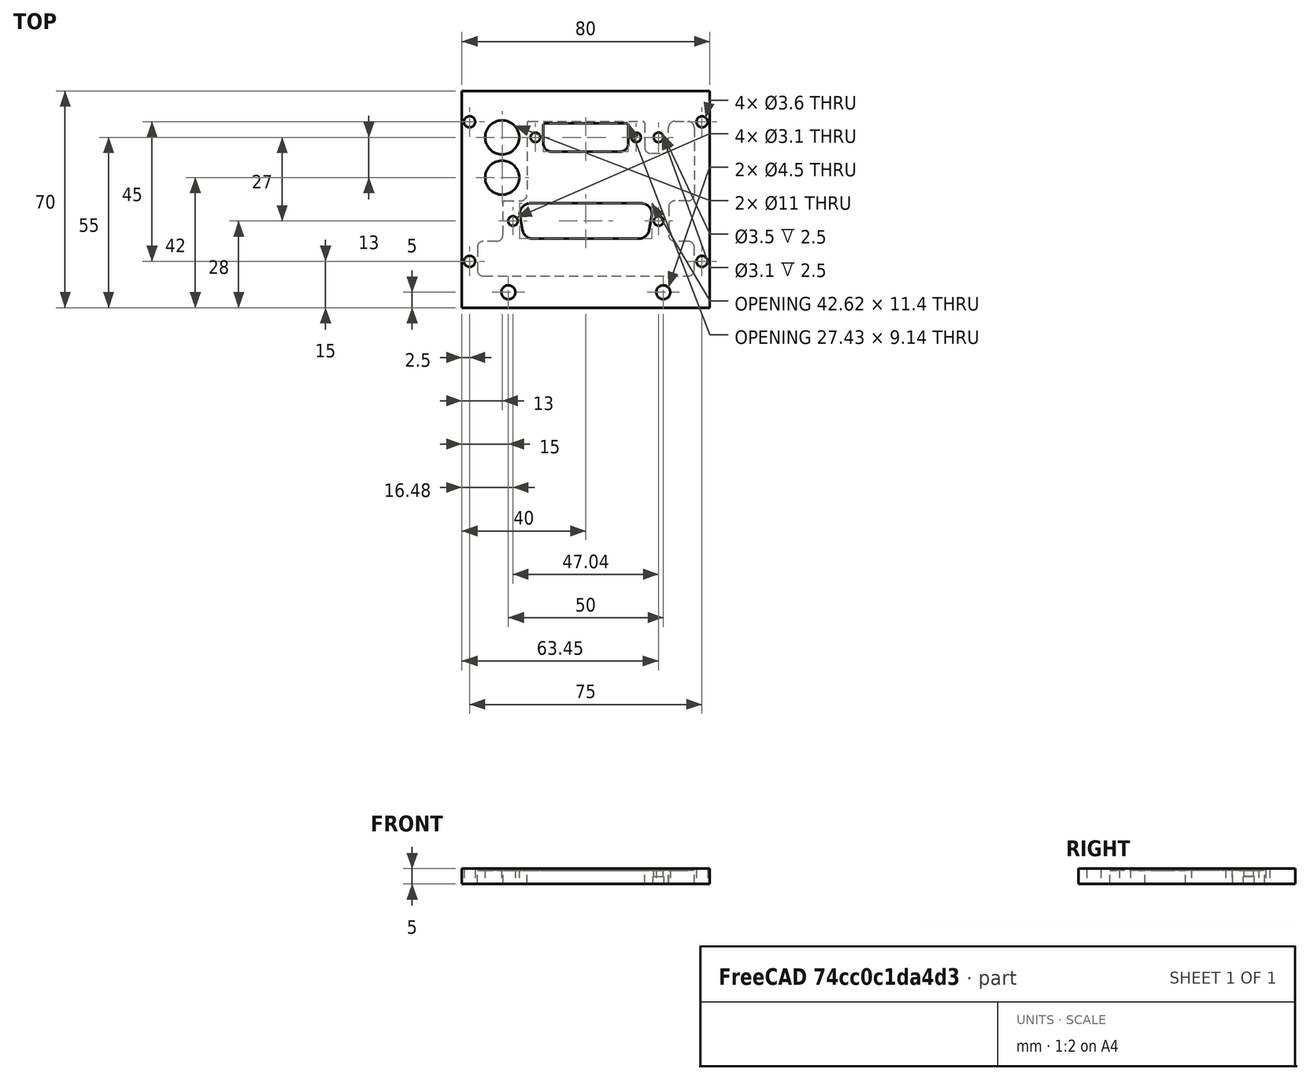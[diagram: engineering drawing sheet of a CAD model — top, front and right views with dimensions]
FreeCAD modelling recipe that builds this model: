
FCSTD DOCUMENT  (FreeCAD 1.0R39319 (Git))
Label: back_panel
License: CERN Open Hardware Licence weakly-reciprocal
LicenseURL: https://cern-ohl.web.cern.ch/
objects: TechDraw::DrawViewDimension×45, Sketcher::SketchObject×8, PartDesign::Hole×5, TechDraw::DrawProjGroupItem×5, TechDraw::DrawSVGTemplate×3, TechDraw::DrawPage×3, PartDesign::Pocket×2, TechDraw::DrawProjGroup×2, PartDesign::Pad×1, PartDesign::Body×1, TechDraw::DrawViewImage×1, TechDraw::DrawViewAnnotation×1, TechDraw::DrawViewSymbol×1
note: 118 computed .brp shape members not serialized (recipe doc carries the construction recipe); baked Part::Feature solids carry a one-line shape summary decoded from their .brp

FEATURE [Sketcher::SketchObject] Sketch
  ArcFitTolerance = 1e-06
  AttachmentSupport = -> [XY_Plane]
  FullyConstrained = true
  MakeInternals = false
  MapMode = 5
  sketch-geometry (5):
    g0: LineSegment StartX=-40 StartY=-35 StartZ=0 EndX=40 EndY=-35 EndZ=0
    g1: LineSegment StartX=40 StartY=-35 StartZ=0 EndX=40 EndY=35 EndZ=0
    g2: LineSegment StartX=40 StartY=35 StartZ=0 EndX=-40 EndY=35 EndZ=0
    g3: LineSegment StartX=-40 StartY=35 StartZ=0 EndX=-40 EndY=-35 EndZ=0
    g4: GeomPoint [constr] X=0 Y=0 Z=0
  constraints (12):
    c: Coincident(g0,g1)
    c: Coincident(g1,g2)
    c: Coincident(g2,g3)
    c: Coincident(g3,g0)
    c: Horizontal(g0)
    c: Horizontal(g2)
    c: Vertical(g1)
    c: Vertical(g3)
    c: Symmetric(g2,g0,g4)
    c: Distance(g1,g3) = 80
    c: Distance(g0,g2) = 70
    c: Coincident(g4,g-1)
FEATURE [PartDesign::Pad] Pad
  Direction = (0,0,1)
  Length = 5
  Length2 = 10
  Profile = -> Sketch
  ReferenceAxis = -> Sketch [N_Axis]
  Suppressed = false
  Type = 0
FEATURE [Sketcher::SketchObject] Sketch001
  ArcFitTolerance = 1e-06
  AttachmentSupport = -> [Pad]
  FullyConstrained = true
  MakeInternals = false
  MapMode = 5
  Placement = pos=(0,0,5) rot=(0,0,1;0rad)
  sketch-geometry (4):
    g0: Circle CenterX=-37.5 CenterY=25 CenterZ=0 NormalX=0 NormalY=0 NormalZ=1 AngleXU=0 Radius=1.7
    g1: Circle CenterX=37.5 CenterY=25 CenterZ=0 NormalX=0 NormalY=0 NormalZ=1 AngleXU=0 Radius=1.7
    g2: Circle CenterX=-37.5 CenterY=-20 CenterZ=0 NormalX=0 NormalY=0 NormalZ=1 AngleXU=0 Radius=1.7
    g3: Circle CenterX=37.5 CenterY=-20 CenterZ=0 NormalX=0 NormalY=0 NormalZ=1 AngleXU=0 Radius=1.7
  constraints (10):
    c: DistanceX(g0,g-1) = 37.5
    c: DistanceY(g-1,g0) = 25
    c: Diameter(g0) = 3.4
    c: Symmetric(g0,g1,g-2)
    c: Equal(g1,g0)
    c: Symmetric(g2,g3,g-2)
    c: Equal(g2,g3)
    c: Equal(g3,g0)
    c: Vertical(g0,g2)
    c: DistanceY(g2,g-1) = 20
FEATURE [PartDesign::Hole] Hole
  BaseFeature = -> Pad
  CustomThreadClearance = 0
  Depth = 214.966
  DepthType = 1
  Diameter = 3.6
  DrillForDepth = false
  DrillPoint = 1
  DrillPointAngle = 118
  HoleCutCountersinkAngle = 90
  HoleCutCustomValues = false
  HoleCutDepth = 0
  HoleCutDiameter = 6.1
  HoleCutType = 0
  ModelThread = false
  Profile = -> Sketch001
  Suppressed = false
  Tapered = false
  TaperedAngle = 90
  ThreadClass = 0
  ThreadDepth = 214.966
  ThreadDepthType = 0
  ThreadDirection = 0
  ThreadFit = 2
  ThreadSize = 9
  ThreadType = 1
  Threaded = false
  UseCustomThreadClearance = false
FEATURE [Sketcher::SketchObject] Sketch005
  ArcFitTolerance = 1e-06
  AttachmentSupport = -> [Hole]
  FullyConstrained = true
  MakeInternals = false
  MapMode = 5
  Placement = pos=(0,0,5) rot=(0,0,1;0rad)
  sketch-geometry (2):
    g0: Circle CenterX=-25 CenterY=-30 CenterZ=0 NormalX=0 NormalY=0 NormalZ=1 AngleXU=0 Radius=2.25
    g1: Circle CenterX=25 CenterY=-30 CenterZ=0 NormalX=0 NormalY=0 NormalZ=1 AngleXU=0 Radius=2.25
  constraints (5):
    c: Symmetric(g1,g0,g-2)
    c: Equal(g0,g1)
    c: DistanceX(g0,g1) = 50
    c: DistanceY(g1,g-1) = 30
    c: Diameter(g0) = 4.5
FEATURE [PartDesign::Hole] Hole003
  BaseFeature = -> Hole
  CustomThreadClearance = 0
  Depth = 214.966
  DepthType = 1
  Diameter = 4.5
  DrillForDepth = false
  DrillPoint = 1
  DrillPointAngle = 118
  HoleCutCountersinkAngle = 90
  HoleCutCustomValues = false
  HoleCutDepth = 0
  HoleCutDiameter = 6.1
  HoleCutType = 0
  ModelThread = false
  Profile = -> Sketch005
  Suppressed = false
  Tapered = false
  TaperedAngle = 90
  ThreadClass = 0
  ThreadDepth = 214.966
  ThreadDepthType = 0
  ThreadDirection = 0
  ThreadFit = 0
  ThreadSize = 0
  ThreadType = 0
  Threaded = false
  UseCustomThreadClearance = false
FEATURE [Sketcher::SketchObject] Sketch003
  ArcFitTolerance = 1e-06
  AttachmentSupport = -> [Hole003]
  FullyConstrained = true
  MakeInternals = false
  MapMode = 5
  Placement = pos=(0,0,5) rot=(0,0,1;0rad)
  sketch-geometry (4):
    g0: Circle CenterX=-16.255 CenterY=20 CenterZ=0 NormalX=0 NormalY=0 NormalZ=1 AngleXU=0 Radius=1.525
    g1: Circle CenterX=16.255 CenterY=20 CenterZ=0 NormalX=0 NormalY=0 NormalZ=1 AngleXU=0 Radius=1.525
    g2: Circle CenterX=-23.52 CenterY=-7 CenterZ=0 NormalX=0 NormalY=0 NormalZ=1 AngleXU=0 Radius=1.525
    g3: Circle CenterX=23.52 CenterY=-7 CenterZ=0 NormalX=0 NormalY=0 NormalZ=1 AngleXU=0 Radius=1.525
  constraints (10):
    c: Diameter(g0) = 3.05
    c: Equal(g1,g0)
    c: DistanceX(g0,g1) = 32.51
    c: DistanceY(g-1,g1) = 20
    c: Equal(g0,g2)
    c: Equal(g2,g3)
    c: DistanceX(g2,g3) = 47.04
    c: DistanceY(g3,g-1) = 7
    c: Symmetric(g0,g1,g-2)
    c: Symmetric(g2,g3,g-2)
FEATURE [PartDesign::Hole] Hole001
  BaseFeature = -> Hole003
  CustomThreadClearance = 0
  Depth = 214.966
  DepthType = 1
  Diameter = 3.1
  DrillForDepth = false
  DrillPoint = 1
  DrillPointAngle = 118
  HoleCutCountersinkAngle = 90
  HoleCutCustomValues = false
  HoleCutDepth = 0
  HoleCutDiameter = 6.1
  HoleCutType = 0
  ModelThread = false
  Profile = -> Sketch003
  Suppressed = false
  Tapered = false
  TaperedAngle = 90
  ThreadClass = 0
  ThreadDepth = 214.966
  ThreadDepthType = 0
  ThreadDirection = 0
  ThreadFit = 0
  ThreadSize = 0
  ThreadType = 0
  Threaded = false
  UseCustomThreadClearance = false
FEATURE [Sketcher::SketchObject] Sketch002
  ArcFitTolerance = 1e-06
  AttachmentSupport = -> [Hole001]
  ExternalGeometry = -> [Hole001]
  FullyConstrained = true
  MakeInternals = false
  MapMode = 5
  Placement = pos=(0,0,5) rot=(0,0,1;0rad)
  sketch-geometry (2):
    g0: Circle CenterX=-27 CenterY=7 CenterZ=0 NormalX=0 NormalY=0 NormalZ=1 AngleXU=0 Radius=5.5
    g1: Circle CenterX=-27 CenterY=20 CenterZ=0 NormalX=0 NormalY=0 NormalZ=1 AngleXU=0 Radius=5.5
  constraints (6):
    c: Equal(g1,g0)
    c: Vertical(g1,g0)
    c: DistanceY(g0,g1) = 13
    c: Diameter(g1) = 11
    c: DistanceX(g0,g-1) = 27
    c: Horizontal(g-3,g1)
FEATURE [PartDesign::Hole] Hole002
  BaseFeature = -> Hole001
  CustomThreadClearance = 0
  Depth = 25
  DepthType = 0
  Diameter = 11
  DrillForDepth = false
  DrillPoint = 1
  DrillPointAngle = 118
  HoleCutCountersinkAngle = 90
  HoleCutCustomValues = false
  HoleCutDepth = 0
  HoleCutDiameter = 6.1
  HoleCutType = 0
  ModelThread = false
  Profile = -> Sketch002
  Suppressed = false
  Tapered = false
  TaperedAngle = 90
  ThreadClass = 0
  ThreadDepth = 25
  ThreadDepthType = 0
  ThreadDirection = 0
  ThreadFit = 0
  ThreadSize = 0
  ThreadType = 0
  Threaded = false
  UseCustomThreadClearance = false
FEATURE [Sketcher::SketchObject] Sketch004
  ArcFitTolerance = 1e-06
  AttachmentSupport = -> [Hole002]
  ExternalGeometry = -> [Hole002]
  FullyConstrained = true
  MakeInternals = false
  MapMode = 5
  Placement = pos=(0,0,5) rot=(0,0,1;0rad)
  sketch-geometry (23):
    g0: LineSegment StartX=-13.715 StartY=23.94 StartZ=0 EndX=-13.715 EndY=17.97 EndZ=0
    g1: LineSegment StartX=-11.175 StartY=15.43 StartZ=0 EndX=11.175 EndY=15.43 EndZ=0
    g2: LineSegment StartX=13.715 StartY=17.97 StartZ=0 EndX=13.715 EndY=23.94 EndZ=0
    g3: LineSegment StartX=13.085 StartY=24.57 StartZ=0 EndX=-13.085 EndY=24.57 EndZ=0
    g4: ArcOfCircle CenterX=-13.085 CenterY=23.94 CenterZ=0 NormalX=0 NormalY=0 NormalZ=1 AngleXU=0 Radius=0.63 StartAngle=1.5708 EndAngle=3.14159
    g5: ArcOfCircle CenterX=-11.175 CenterY=17.97 CenterZ=0 NormalX=0 NormalY=0 NormalZ=1 AngleXU=0 Radius=2.54 StartAngle=3.14159 EndAngle=4.71239
    g6: ArcOfCircle CenterX=11.175 CenterY=17.97 CenterZ=0 NormalX=0 NormalY=0 NormalZ=1 AngleXU=0 Radius=2.54 StartAngle=4.71239 EndAngle=6.28319
    g7: ArcOfCircle CenterX=13.085 CenterY=23.94 CenterZ=0 NormalX=0 NormalY=0 NormalZ=1 AngleXU=0 Radius=0.63 StartAngle=2.2e-15 EndAngle=1.5708
    g8: GeomPoint [constr] X=-13.715 Y=24.57 Z=0
    g9: GeomPoint [constr] X=13.715 Y=15.43 Z=0
    g10: LineSegment StartX=-21.26 StartY=-5.23172 StartZ=0 EndX=-20.4313 EndY=-9.93172 EndZ=0
    g11: LineSegment StartX=-17.1322 StartY=-12.7 StartZ=0 EndX=17.1322 EndY=-12.7 EndZ=0
    g12: LineSegment StartX=20.4313 StartY=-9.93172 StartZ=0 EndX=21.26 EndY=-5.23172 EndZ=0
    g13: LineSegment StartX=17.9609 StartY=-1.3 StartZ=0 EndX=-17.9609 EndY=-1.3 EndZ=0
    g14: ArcOfCircle CenterX=-17.9609 CenterY=-4.65 CenterZ=0 NormalX=0 NormalY=0 NormalZ=1 AngleXU=0 Radius=3.35 StartAngle=1.5708 EndAngle=3.31613
    g15: ArcOfCircle CenterX=-17.1322 CenterY=-9.35 CenterZ=0 NormalX=0 NormalY=0 NormalZ=1 AngleXU=0 Radius=3.35 StartAngle=3.31613 EndAngle=4.71239
    g16: ArcOfCircle CenterX=17.1322 CenterY=-9.35 CenterZ=0 NormalX=0 NormalY=0 NormalZ=1 AngleXU=0 Radius=3.35 StartAngle=4.71239 EndAngle=6.10865
    g17: ArcOfCircle CenterX=17.9609 CenterY=-4.65 CenterZ=0 NormalX=0 NormalY=0 NormalZ=1 AngleXU=0 Radius=3.35 StartAngle=6.10865 EndAngle=7.85398
    g18: GeomPoint [constr] X=19.9431 Y=-12.7 Z=0
    g19: LineSegment [constr] StartX=16.255 StartY=20 StartZ=0 EndX=-16.255 EndY=20 EndZ=0
    g20: LineSegment [constr] StartX=-23.52 StartY=-7 StartZ=0 EndX=23.52 EndY=-7 EndZ=0
    g21: LineSegment [constr] StartX=-9e-16 StartY=-1.3 StartZ=0 EndX=-9e-16 EndY=-12.7 EndZ=0
    g22: GeomPoint [constr] X=13.715 Y=24.57 Z=0
  constraints (51):
    c: Tangent(g0,g4) = -1.5708
    c: Tangent(g0,g5) = -1.5708
    c: Tangent(g1,g5) = -1.5708
    c: Tangent(g1,g6) = -1.5708
    c: Tangent(g2,g6) = -1.5708
    c: Tangent(g2,g7) = -1.5708
    c: Tangent(g3,g7) = -1.5708
    c: Tangent(g3,g4) = -1.5708
    c: Vertical(g0)
    c: Horizontal(g1)
    c: Horizontal(g3)
    c: PointOnObject(g8,g0)
    c: PointOnObject(g8,g3)
    c: PointOnObject(g9,g1)
    c: PointOnObject(g9,g2)
    c: Radius(g5) = 2.54
    c: Radius(g4) = 0.63
    c: Distance(g1,g3) = 9.14
    c: Tangent(g10,g14) = -1.5708
    c: Tangent(g10,g15) = -1.5708
    c: Tangent(g11,g15) = -1.5708
    c: Tangent(g11,g16) = -1.5708
    c: Tangent(g12,g16) = -1.5708
    c: Tangent(g12,g17) = -1.5708
    c: Tangent(g13,g17) = -1.5708
    c: Tangent(g13,g14) = -1.5708
    c: Horizontal(g11)
    c: Horizontal(g13)
    c: Equal(g15,g16)
    c: PointOnObject(g18,g11)
    c: PointOnObject(g18,g12)
    c: Symmetric(g12,g10,g-2)
    c: Radius(g14) = 3.35
    c: Equal(g14,g17)
    c: DistanceY(g11,g13) = 11.4
    c: DistanceX(g10,g12) = 42.52
    c: Equal(g17,g15)
    c: Coincident(g19,g-4)
    c: Coincident(g19,g-3)
    c: Coincident(g20,g-5)
    c: Coincident(g20,g-6)
    c: Symmetric(g0,g2,g-2)
    c: Equal(g7,g4)
    c: PointOnObject(g21,g13)
    c: Symmetric(g21,g21,g20)
    c: Symmetric(g11,g11,g21)
    c: DistanceX(g0,g2) = 27.43
    c: PointOnObject(g22,g2)
    c: PointOnObject(g22,g3)
    c: Symmetric(g22,g9,g19)
    c: Angle(g12,g-2) = 0.174533
FEATURE [PartDesign::Pocket] Pocket
  BaseFeature = -> Hole002
  Direction = (0,0,-1)
  Length = 5
  Length2 = 5
  Profile = -> Sketch004
  ReferenceAxis = -> Sketch004 [N_Axis]
  Suppressed = false
  Type = 1
FEATURE [Sketcher::SketchObject] Sketch006
  ArcFitTolerance = 1e-06
  AttachmentSupport = -> [Pocket]
  ExternalGeometry = -> [Pocket]
  FullyConstrained = true
  MakeInternals = false
  MapMode = 5
  Placement = pos=(0,0,0) rot=(1,0,0;3.14159rad)
  sketch-geometry (1):
    g0: Circle CenterX=23.45 CenterY=-20 CenterZ=0 NormalX=0 NormalY=0 NormalZ=1 AngleXU=0 Radius=1.75
  constraints (3):
    c: Diameter(g0) = 3.5
    c: Horizontal(g0,g-3)
    c: DistanceX(g-1,g0) = 23.45
FEATURE [PartDesign::Hole] Hole004
  BaseFeature = -> Pocket
  CustomThreadClearance = 0
  Depth = 214.966
  DepthType = 1
  Diameter = 3.1
  DrillForDepth = false
  DrillPoint = 1
  DrillPointAngle = 118
  HoleCutCountersinkAngle = 90
  HoleCutCustomValues = false
  HoleCutDepth = 2.5
  HoleCutDiameter = 3.5
  HoleCutType = 1
  ModelThread = false
  Profile = -> Sketch006
  Suppressed = false
  Tapered = false
  TaperedAngle = 90
  ThreadClass = 0
  ThreadDepth = 214.966
  ThreadDepthType = 0
  ThreadDirection = 0
  ThreadFit = 0
  ThreadSize = 0
  ThreadType = 0
  Threaded = false
  UseCustomThreadClearance = false
FEATURE [Sketcher::SketchObject] Sketch007
  ArcFitTolerance = 1e-06
  AttachmentSupport = -> [Hole004]
  ExternalGeometry = -> [Hole004]
  FullyConstrained = true
  MakeInternals = false
  MapMode = 5
  Placement = pos=(0,0,0) rot=(1,0,0;3.14159rad)
  expr: Constraints[100] = 9.8 mm + 0.5 mm
  expr: Constraints[52] = 37.5 mm + 0.5 mm
  expr: Constraints[78] = 12.55 mm + 0.5 mm
  sketch-geometry (55):
    g0: LineSegment StartX=-18.4 StartY=-25.15 StartZ=0 EndX=18.4 EndY=-25.15 EndZ=0
    g1: LineSegment StartX=19 StartY=-24.55 StartZ=0 EndX=19 EndY=-16.85 EndZ=0
    g2: LineSegment StartX=26.75 StartY=2.475 StartZ=0 EndX=26.75 EndY=11.525 EndZ=0
    g3: LineSegment StartX=-26.75 StartY=11.525 StartZ=0 EndX=-26.75 EndY=1.075 EndZ=0
    g4: LineSegment StartX=-26.15 StartY=0.475 StartZ=0 EndX=-21 EndY=0.475 EndZ=0
    g5: LineSegment StartX=-19 StartY=-24.55 StartZ=0 EndX=-19 EndY=-1.525 EndZ=0
    g6: ArcOfCircle CenterX=21 CenterY=-16.85 CenterZ=0 NormalX=0 NormalY=0 NormalZ=1 AngleXU=0 Radius=2 StartAngle=1.5708 EndAngle=3.14159
    g7: GeomPoint [constr] X=19 Y=-14.85 Z=0
    g8: ArcOfCircle CenterX=18.4 CenterY=-24.55 CenterZ=0 NormalX=0 NormalY=0 NormalZ=1 AngleXU=0 Radius=0.6 StartAngle=4.71239 EndAngle=6.28319
    g9: GeomPoint [constr] X=19 Y=-25.15 Z=0
    g10: ArcOfCircle CenterX=-18.4 CenterY=-24.55 CenterZ=0 NormalX=0 NormalY=0 NormalZ=1 AngleXU=0 Radius=0.6 StartAngle=3.14159 EndAngle=4.71239
    g11: GeomPoint [constr] X=-19 Y=-25.15 Z=0
    g12: ArcOfCircle CenterX=-21 CenterY=-1.525 CenterZ=0 NormalX=0 NormalY=0 NormalZ=1 AngleXU=0 Radius=2 StartAngle=0 EndAngle=1.5708
    g13: GeomPoint [constr] X=-19 Y=0.475 Z=0
    g14: ArcOfCircle CenterX=-26.15 CenterY=1.075 CenterZ=0 NormalX=0 NormalY=0 NormalZ=1 AngleXU=0 Radius=0.6 StartAngle=3.14159 EndAngle=4.71239
    g15: GeomPoint [constr] X=-26.75 Y=0.475 Z=0
    g16: LineSegment StartX=-28.75 StartY=13.525 StartZ=0 EndX=-33 EndY=13.525 EndZ=0
    g17: LineSegment StartX=-35 StartY=15.525 StartZ=0 EndX=-35 EndY=22.775 EndZ=0
    g18: LineSegment StartX=-33 StartY=24.775 StartZ=0 EndX=33 EndY=24.775 EndZ=0
    g19: LineSegment StartX=35 StartY=22.775 StartZ=0 EndX=35 EndY=15.525 EndZ=0
    g20: LineSegment StartX=33 StartY=13.525 StartZ=0 EndX=28.75 EndY=13.525 EndZ=0
    g21: ArcOfCircle CenterX=-28.75 CenterY=11.525 CenterZ=0 NormalX=0 NormalY=0 NormalZ=1 AngleXU=0 Radius=2 StartAngle=0 EndAngle=1.5708
    g22: GeomPoint [constr] X=-26.75 Y=13.525 Z=0
    g23: ArcOfCircle CenterX=-33 CenterY=15.525 CenterZ=0 NormalX=0 NormalY=0 NormalZ=1 AngleXU=0 Radius=2 StartAngle=3.14159 EndAngle=4.71239
    g24: GeomPoint [constr] X=-35 Y=13.525 Z=0
    g25: ArcOfCircle CenterX=-33 CenterY=22.775 CenterZ=0 NormalX=0 NormalY=0 NormalZ=1 AngleXU=0 Radius=2 StartAngle=1.5708 EndAngle=3.14159
    g26: GeomPoint [constr] X=-35 Y=24.775 Z=0
    g27: ArcOfCircle CenterX=33 CenterY=22.775 CenterZ=0 NormalX=0 NormalY=0 NormalZ=1 AngleXU=0 Radius=2 StartAngle=0 EndAngle=1.5708
    g28: GeomPoint [constr] X=35 Y=24.775 Z=0
    g29: ArcOfCircle CenterX=33 CenterY=15.525 CenterZ=0 NormalX=0 NormalY=0 NormalZ=1 AngleXU=0 Radius=2 StartAngle=4.71239 EndAngle=6.28319
    g30: GeomPoint [constr] X=35 Y=13.525 Z=0
    g31: ArcOfCircle CenterX=28.75 CenterY=11.525 CenterZ=0 NormalX=0 NormalY=0 NormalZ=1 AngleXU=0 Radius=2 StartAngle=1.5708 EndAngle=3.14159
    g32: LineSegment StartX=35 StartY=-23.15 StartZ=0 EndX=35 EndY=-1.525 EndZ=0
    g33: LineSegment StartX=33 StartY=0.475 StartZ=0 EndX=28.75 EndY=0.475 EndZ=0
    g34: ArcOfCircle CenterX=33 CenterY=-23.15 CenterZ=0 NormalX=0 NormalY=0 NormalZ=1 AngleXU=0 Radius=2 StartAngle=4.71239 EndAngle=6.28319
    g35: GeomPoint [constr] X=35 Y=-25.15 Z=0
    g36: ArcOfCircle CenterX=33 CenterY=-1.525 CenterZ=0 NormalX=0 NormalY=0 NormalZ=1 AngleXU=0 Radius=2 StartAngle=0 EndAngle=1.5708
    g37: GeomPoint [constr] X=35 Y=0.475 Z=0
    g38: ArcOfCircle CenterX=28.75 CenterY=2.475 CenterZ=0 NormalX=0 NormalY=0 NormalZ=1 AngleXU=0 Radius=2 StartAngle=3.14159 EndAngle=4.71239
    g39: GeomPoint [constr] X=26.75 Y=0.475 Z=0
    g40: LineSegment [constr] StartX=16.255 StartY=-20 StartZ=0 EndX=-19 EndY=-20 EndZ=0
    g41: LineSegment [constr] StartX=23.52 StartY=7 StartZ=0 EndX=-26.75 EndY=7 EndZ=0
    g42: GeomPoint [constr] X=26.75 Y=13.525 Z=0
    g43: LineSegment StartX=21 StartY=-14.85 StartZ=0 EndX=24.7 EndY=-14.85 EndZ=0
    g44: LineSegment StartX=26.7 StartY=-16.85 StartZ=0 EndX=26.7 EndY=-23.15 EndZ=0
    g45: LineSegment StartX=28.7 StartY=-25.15 StartZ=0 EndX=33 EndY=-25.15 EndZ=0
    g46: ArcOfCircle CenterX=24.7 CenterY=-16.85 CenterZ=0 NormalX=0 NormalY=0 NormalZ=1 AngleXU=0 Radius=2 StartAngle=0 EndAngle=1.5708
    g47: GeomPoint [constr] X=26.7 Y=-14.85 Z=0
    g48: ArcOfCircle CenterX=28.7 CenterY=-23.15 CenterZ=0 NormalX=0 NormalY=0 NormalZ=1 AngleXU=0 Radius=2 StartAngle=3.14159 EndAngle=4.71239
    g49: GeomPoint [constr] X=26.7 Y=-25.15 Z=0
    g50: LineSegment [constr] StartX=28.7 StartY=-19.2 StartZ=0 EndX=28.7 EndY=-20.8 EndZ=0
    g51: LineSegment [constr] StartX=28.7 StartY=-20.8 StartZ=0 EndX=30.3 EndY=-20.8 EndZ=0
    g52: LineSegment [constr] StartX=30.3 StartY=-20.8 StartZ=0 EndX=30.3 EndY=-19.2 EndZ=0
    g53: LineSegment [constr] StartX=30.3 StartY=-19.2 StartZ=0 EndX=28.7 EndY=-19.2 EndZ=0
    g54: GeomPoint [constr] X=29.5 Y=-20 Z=0
  constraints (126):
    c: Horizontal(g0)
    c: Vertical(g1)
    c: Vertical(g2)
    c: Vertical(g3)
    c: Horizontal(g4)
    c: Vertical(g5)
    c: PointOnObject(g7,g1)
    c: Tangent(g1,g6) = 1.5708
    c: PointOnObject(g9,g0)
    c: PointOnObject(g9,g1)
    c: Tangent(g0,g8) = -1.5708
    c: Tangent(g1,g8) = -1.5708
    c: PointOnObject(g11,g0)
    c: PointOnObject(g11,g5)
    c: Tangent(g0,g10) = -1.5708
    c: Tangent(g5,g10) = 1.5708
    c: PointOnObject(g13,g4)
    c: PointOnObject(g13,g5)
    c: Tangent(g4,g12) = 1.5708
    c: Tangent(g5,g12) = -1.5708
    c: PointOnObject(g15,g3)
    c: PointOnObject(g15,g4)
    c: Tangent(g3,g14) = -1.5708
    c: Tangent(g4,g14) = -1.5708
    c: Radius(g8) = 0.6
    c: Horizontal(g16)
    c: Vertical(g17)
    c: Horizontal(g18)
    c: Vertical(g19)
    c: Horizontal(g20)
    c: PointOnObject(g22,g3)
    c: PointOnObject(g22,g16)
    c: Tangent(g3,g21) = 1.5708
    c: Tangent(g16,g21) = -1.5708
    c: PointOnObject(g24,g16)
    c: PointOnObject(g24,g17)
    c: Tangent(g16,g23) = 1.5708
    c: Tangent(g17,g23) = 1.5708
    c: PointOnObject(g26,g17)
    c: PointOnObject(g26,g18)
    c: Tangent(g17,g25) = 1.5708
    c: Tangent(g18,g25) = 1.5708
    c: PointOnObject(g28,g18)
    c: PointOnObject(g28,g19)
    c: Tangent(g18,g27) = 1.5708
    c: Tangent(g19,g27) = 1.5708
    c: PointOnObject(g30,g19)
    c: PointOnObject(g30,g20)
    c: Tangent(g19,g29) = 1.5708
    c: Tangent(g20,g29) = 1.5708
    c: Tangent(g2,g31) = 1.5708
    c: Tangent(g20,g31) = -1.5708
    c: DistanceX(g5,g1) = 38
    c: DistanceX(g17,g19) = 70
    c: Equal(g25,g23)
    c: Equal(g27,g29)
    c: Equal(g14,g10)
    c: Radius(g25) = 2
    c: DistanceY(g16,g18) = 11.25
    c: Vertical(g32)
    c: Horizontal(g33)
    c: PointOnObject(g35,g32)
    c: Tangent(g32,g34) = -1.5708
    c: PointOnObject(g37,g32)
    c: PointOnObject(g37,g33)
    c: Tangent(g32,g36) = -1.5708
    c: Tangent(g33,g36) = -1.5708
    c: PointOnObject(g39,g2)
    c: PointOnObject(g39,g33)
    c: Tangent(g2,g38) = 1.5708
    c: Tangent(g33,g38) = 1.5708
    c: Equal(g34,g36)
    c: Equal(g36,g29)
    c: Equal(g38,g36)
    c: Equal(g31,g38)
    c: Equal(g21,g12)
    c: Equal(g34,g6)
    c: DistanceX(g5,g32) = 54
    c: Distance(g33,g20) = 13.05
    c: Equal(g25,g21)
    c: Symmetric(g21,g31,g-2)
    c: Symmetric(g10,g8,g-2)
    c: Distance(g3,g2) = 53.5
    c: Symmetric(g25,g27,g-2)
    c: Coincident(g40,g-3)
    c: Symmetric(g7,g9,g40)
    c: PointOnObject(g40,g5)
    c: Coincident(g41,g-4)
    c: PointOnObject(g41,g3)
    c: Horizontal(g41)
    c: PointOnObject(g42,g20)
    c: Symmetric(g42,g39,g41)
    c: Horizontal(g43)
    c: Tangent(g43,g6) = 1.5708
    c: Vertical(g44)
    c: Horizontal(g45)
    c: PointOnObject(g47,g43)
    c: PointOnObject(g47,g44)
    c: Tangent(g43,g46) = 1.5708
    c: Tangent(g44,g46) = 1.5708
    c: DistanceY(g9,g47) = 10.3
    c: Tangent(g45,g34) = -1.5708
    c: PointOnObject(g49,g44)
    c: PointOnObject(g49,g45)
    c: Tangent(g44,g48) = -1.5708
    c: Tangent(g45,g48) = -1.5708
    c: Equal(g48,g34)
    c: Horizontal(g49,g9)
    c: Equal(g46,g6)
    c: PointOnObject(g7,g43)
    c: PointOnObject(g35,g45)
    c: Coincident(g50,g51)
    c: Coincident(g51,g52)
    c: Coincident(g52,g53)
    c: Coincident(g53,g50)
    c: Vertical(g50)
    c: Vertical(g52)
    c: Horizontal(g51)
    c: Horizontal(g53)
    c: Symmetric(g52,g50,g54)
    c: Equal(g52,g53)
    c: DistanceX(g53,g53) = 1.6
    c: PointOnObject(g54,g40)
    c: Distance(g54,g-2) = 29.5
    c: DistanceX(g44,g50) = 2
    c: Horizontal(g13,g39)
FEATURE [PartDesign::Pocket] Pocket001
  BaseFeature = -> Hole004
  Direction = (0,0,1)
  Length = 4.4
  Length2 = 5
  Profile = -> Sketch007
  ReferenceAxis = -> Sketch007 [N_Axis]
  Suppressed = false
  Type = 0
FEATURE [PartDesign::Body] Body
  AllowCompound = false
  Group = -> [Sketch,Pad,Sketch001,Hole,Hole003,Sketch003,Hole001,Sketch002,Hole002,Sketch004,Pocket,Sketch005,Sketch006,Hole004,Sketch007,Pocket001]
  Origin = -> Origin
  Tip = -> Pocket001
FEATURE [TechDraw::DrawSVGTemplate] Template
  EditableTexts = approval_person=Patrick Baus; creator=Patrick Baus; date_of_issue=31.08.25; document_type=Component Drawing; general_tolerances=ISO 2768-m; identification_number=DN; language_code=EN; legal_owner_1=Quantum Electronic; legal_owner_2=Devices GmbH; legal_owner_3=CERN-OHL-W-2.0; part_material=Aluminium; revision_index=2.1.0; scale=1 : 1; sheet_number=1 / 3; title=Laser back panel
  Height = 210
  Orientation = 1
  Template = <path>
  Width = 297
FEATURE [TechDraw::DrawProjGroupItem] View  label="Front"
  CoarseView = false
  Direction = (0,0,1)
  Focus = 100
  HardHidden = true
  IsoCount = 0
  IsoHidden = false
  IsoVisible = false
  LockPosition = true
  Perspective = false
  Rotation = 0
  RotationVector = (1,0,0)
  ScaleType = 2
  ScrubCount = 1
  SeamHidden = false
  SeamVisible = false
  SmoothHidden = false
  SmoothVisible = true
  Source = -> [Body]
  Type = 0
  X = 0
  XDirection = (1,-1e-16,2e-16)
  Y = 0
FEATURE [TechDraw::DrawViewDimension] Dimension008
  AngleOverride = false
  Arbitrary = false
  ArbitraryTolerances = false
  BoxCorners = (2) [(-40,-35,0),(40,35,0)]
  EqualTolerance = true
  ExtensionAngle = 0
  FormatSpec = ⌀%.2f THRU
  FormatSpecOverTolerance = %+.2w
  FormatSpecUnderTolerance = %+.2w
  Inverted = false
  LineAngle = 0
  LockPosition = false
  MeasureType = 1
  OverTolerance = 0
  References2D = -> [View]
  Rotation = 0
  ScaleType = 0
  TheoreticalExact = false
  Type = 5
  UnderTolerance = 0
  X = -20.5797
  Y = 45.8459
FEATURE [TechDraw::DrawViewDimension] Dimension009
  AngleOverride = false
  Arbitrary = false
  ArbitraryTolerances = false
  BoxCorners = (2) [(-40,-35,0),(40,35,0)]
  EqualTolerance = true
  ExtensionAngle = 0
  FormatSpec = ⌀%.2f THRU
  FormatSpecOverTolerance = %+.2w
  FormatSpecUnderTolerance = %+.2w
  Inverted = false
  LineAngle = 0
  LockPosition = false
  MeasureType = 1
  OverTolerance = 0
  References2D = -> [View]
  Rotation = 0
  ScaleType = 0
  TheoreticalExact = false
  Type = 5
  UnderTolerance = 0
  X = -7.48623
  Y = 44.6513
FEATURE [TechDraw::DrawViewDimension] Dimension012
  AngleOverride = false
  Arbitrary = false
  ArbitraryTolerances = false
  BoxCorners = (2) [(-40,-35,0),(40,35,0)]
  EqualTolerance = true
  ExtensionAngle = 0
  FormatSpec = %.2f
  FormatSpecOverTolerance = %+.2w
  FormatSpecUnderTolerance = %+.2w
  Inverted = false
  LineAngle = 0
  LockPosition = false
  MeasureType = 1
  OverTolerance = 0
  References2D = -> [View]
  Rotation = 0
  ScaleType = 0
  TheoreticalExact = false
  Type = 1
  UnderTolerance = 0
  X = 0
  Y = -45.1409
FEATURE [TechDraw::DrawViewDimension] Dimension013
  AngleOverride = false
  Arbitrary = false
  ArbitraryTolerances = false
  BoxCorners = (2) [(-40,-35,0),(40,35,0)]
  EqualTolerance = true
  ExtensionAngle = 0
  FormatSpec = %.2f
  FormatSpecOverTolerance = %+.2w
  FormatSpecUnderTolerance = %+.2w
  Inverted = false
  LineAngle = 0
  LockPosition = false
  MeasureType = 1
  OverTolerance = 0
  References2D = -> [View]
  Rotation = 0
  ScaleType = 0
  TheoreticalExact = false
  Type = 1
  UnderTolerance = 0
  X = 0
  Y = -59.1409
FEATURE [TechDraw::DrawViewDimension] Dimension
  AngleOverride = false
  Arbitrary = false
  ArbitraryTolerances = false
  BoxCorners = (2) [(-40,-35,0),(40,35,0)]
  EqualTolerance = true
  ExtensionAngle = 0
  FormatSpec = %.2f
  FormatSpecOverTolerance = %+.2w
  FormatSpecUnderTolerance = %+.2w
  Inverted = false
  LineAngle = 0
  LockPosition = false
  MeasureType = 1
  OverTolerance = 0
  References2D = -> [View]
  Rotation = 0
  ScaleType = 0
  TheoreticalExact = false
  Type = 0
  UnderTolerance = 0
  X = 41.4534
  Y = 30
FEATURE [TechDraw::DrawViewDimension] Dimension014
  AngleOverride = false
  Arbitrary = false
  ArbitraryTolerances = false
  BoxCorners = (2) [(-40,-35,0),(40,35,0)]
  EqualTolerance = true
  ExtensionAngle = 0
  FormatSpec = %.2f
  FormatSpecOverTolerance = %+.2w
  FormatSpecUnderTolerance = %+.2w
  Inverted = false
  LineAngle = 0
  LockPosition = false
  MeasureType = 1
  OverTolerance = 0
  References2D = -> [View]
  Rotation = 0
  ScaleType = 0
  TheoreticalExact = false
  Type = 0
  UnderTolerance = 0
  X = 65.6288
  Y = 7.5
FEATURE [TechDraw::DrawViewDimension] Dimension015
  AngleOverride = false
  Arbitrary = false
  ArbitraryTolerances = false
  BoxCorners = (2) [(-40,-35,0),(40,35,0)]
  EqualTolerance = true
  ExtensionAngle = 0
  FormatSpec = %.2f
  FormatSpecOverTolerance = %+.2w
  FormatSpecUnderTolerance = %+.2w
  Inverted = false
  LineAngle = 0
  LockPosition = false
  MeasureType = 1
  OverTolerance = 0
  References2D = -> [View]
  Rotation = 0
  ScaleType = 0
  TheoreticalExact = false
  Type = 0
  UnderTolerance = 0
  X = -8.275
  Y = 60.9727
FEATURE [TechDraw::DrawViewDimension] Dimension016
  AngleOverride = false
  Arbitrary = false
  ArbitraryTolerances = false
  BoxCorners = (2) [(-40,-35,0),(40,35,0)]
  EqualTolerance = true
  ExtensionAngle = 0
  FormatSpec = %.2f
  FormatSpecOverTolerance = %+.2w
  FormatSpecUnderTolerance = %+.2w
  Inverted = false
  LineAngle = 0
  LockPosition = false
  MeasureType = 1
  OverTolerance = 0
  References2D = -> [View]
  Rotation = 0
  ScaleType = 0
  TheoreticalExact = false
  Type = 1
  UnderTolerance = 0
  X = 0
  Y = -52.1409
FEATURE [TechDraw::DrawViewDimension] Dimension017
  AngleOverride = false
  Arbitrary = false
  ArbitraryTolerances = false
  BoxCorners = (2) [(-40,-35,0),(40,35,0)]
  EqualTolerance = true
  ExtensionAngle = 0
  FormatSpec = %.2f
  FormatSpecOverTolerance = %+.2w
  FormatSpecUnderTolerance = %+.2w
  Inverted = false
  LineAngle = 0
  LockPosition = false
  MeasureType = 1
  OverTolerance = 0
  References2D = -> [View]
  Rotation = 0
  ScaleType = 0
  TheoreticalExact = false
  Type = 0
  UnderTolerance = 0
  X = -45.3715
  Y = 27.5
FEATURE [TechDraw::DrawViewDimension] Dimension018
  AngleOverride = false
  Arbitrary = false
  ArbitraryTolerances = false
  BoxCorners = (2) [(-40,-35,0),(40,35,0)]
  EqualTolerance = true
  ExtensionAngle = 0
  FormatSpec = %.2f
  FormatSpecOverTolerance = %+.2w
  FormatSpecUnderTolerance = %+.2w
  Inverted = false
  LineAngle = 0
  LockPosition = false
  MeasureType = 1
  OverTolerance = 0
  References2D = -> [View]
  Rotation = 0
  ScaleType = 0
  TheoreticalExact = false
  Type = 0
  UnderTolerance = 0
  X = -52.3715
  Y = 21
FEATURE [TechDraw::DrawViewDimension] Dimension019
  AngleOverride = false
  Arbitrary = false
  ArbitraryTolerances = false
  BoxCorners = (2) [(-40,-35,0),(40,35,0)]
  EqualTolerance = true
  ExtensionAngle = 0
  FormatSpec = %.2f
  FormatSpecOverTolerance = %+.2w
  FormatSpecUnderTolerance = %+.2w
  Inverted = false
  LineAngle = 0
  LockPosition = false
  MeasureType = 1
  OverTolerance = 0
  References2D = -> [View]
  Rotation = 0
  ScaleType = 0
  TheoreticalExact = false
  Type = 0
  UnderTolerance = 0
  X = -33.5
  Y = 53.9727
FEATURE [TechDraw::DrawViewDimension] Dimension020
  AngleOverride = false
  Arbitrary = false
  ArbitraryTolerances = false
  BoxCorners = (2) [(-40,-35,0),(40,35,0)]
  EqualTolerance = true
  ExtensionAngle = 0
  FormatSpec = %.2f
  FormatSpecOverTolerance = %+.2w
  FormatSpecUnderTolerance = %+.2w
  Inverted = false
  LineAngle = 0
  LockPosition = false
  MeasureType = 1
  OverTolerance = 0
  References2D = -> [View]
  Rotation = 0
  ScaleType = 0
  TheoreticalExact = false
  Type = 0
  UnderTolerance = 0
  X = 53.3808
  Y = 27.5
FEATURE [TechDraw::DrawViewDimension] Dimension021
  AngleOverride = false
  Arbitrary = false
  ArbitraryTolerances = false
  BoxCorners = (2) [(-40,-35,0),(40,35,0)]
  EqualTolerance = true
  ExtensionAngle = 0
  FormatSpec = %.2f
  FormatSpecOverTolerance = %+.2w
  FormatSpecUnderTolerance = %+.2w
  Inverted = false
  LineAngle = 0
  LockPosition = false
  MeasureType = 1
  OverTolerance = 0
  References2D = -> [View]
  Rotation = 0
  ScaleType = 0
  TheoreticalExact = false
  Type = 0
  UnderTolerance = 0
  X = 60.3808
  Y = 14
FEATURE [TechDraw::DrawProjGroupItem] ProjItem  label="Left"
  CoarseView = false
  Direction = (-1,1e-16,1e-16)
  Focus = 100
  HardHidden = true
  IsoCount = 0
  IsoHidden = false
  IsoVisible = false
  LockPosition = false
  Perspective = false
  Rotation = 0
  RotationVector = (1,0,0)
  ScaleType = 0
  ScrubCount = 1
  SeamHidden = false
  SeamVisible = false
  SmoothHidden = false
  SmoothVisible = true
  Source = -> [Body]
  Type = 1
  X = 92.5
  XDirection = (1e-16,0,1)
  Y = 0
FEATURE [TechDraw::DrawProjGroup] ProjGroup
  Anchor = -> View
  AutoDistribute = true
  LockPosition = false
  ProjectionType = 0
  Rotation = 0
  ScaleType = 0
  Source = -> [Body]
  Views = -> [View,ProjItem]
  X = 167.028
  Y = 133.106
  spacingX = 50
  spacingY = 15
FEATURE [TechDraw::DrawViewDimension] Dimension023
  AngleOverride = false
  Arbitrary = false
  ArbitraryTolerances = false
  BoxCorners = (2) [(-2.5,-35,0),(2.5,35,0)]
  EqualTolerance = true
  ExtensionAngle = 0
  FormatSpec = %.2f
  FormatSpecOverTolerance = %+.2w
  FormatSpecUnderTolerance = %+.2w
  Inverted = false
  LineAngle = 0
  LockPosition = false
  MeasureType = 1
  OverTolerance = 0
  References2D = -> [ProjItem]
  Rotation = 0
  ScaleType = 0
  TheoreticalExact = false
  Type = 1
  UnderTolerance = 0
  X = -7.47495
  Y = 48.0731
FEATURE [TechDraw::DrawViewDimension] Dimension024
  AngleOverride = false
  Arbitrary = false
  ArbitraryTolerances = false
  BoxCorners = (2) [(-40,-35,0),(40,35,0)]
  EqualTolerance = true
  ExtensionAngle = 0
  FormatSpec = %.2f
  FormatSpecOverTolerance = %+.2w
  FormatSpecUnderTolerance = %+.2w
  Inverted = false
  LineAngle = 0
  LockPosition = false
  MeasureType = 1
  OverTolerance = 0
  References2D = -> [View]
  Rotation = 0
  ScaleType = 0
  TheoreticalExact = false
  Type = 0
  UnderTolerance = 0
  X = 72.6288
  Y = 2.5
FEATURE [TechDraw::DrawViewDimension] Dimension025
  AngleOverride = false
  Arbitrary = false
  ArbitraryTolerances = false
  BoxCorners = (2) [(-40,-35,0),(40,35,0)]
  EqualTolerance = true
  ExtensionAngle = 0
  FormatSpec = %.2f
  FormatSpecOverTolerance = %+.2w
  FormatSpecUnderTolerance = %+.2w
  Inverted = false
  LineAngle = 0
  LockPosition = false
  MeasureType = 1
  OverTolerance = 0
  References2D = -> [View]
  Rotation = 0
  ScaleType = 0
  TheoreticalExact = false
  Type = 0
  UnderTolerance = 0
  X = 79.6288
  Y = 0
FEATURE [TechDraw::DrawSVGTemplate] Template001
  EditableTexts = approval_person=Patrick Baus; creator=Patrick Baus; date_of_issue=31.08.25; document_type=Component Drawing; general_tolerances=ISO 2768-m; identification_number=DN; language_code=EN; legal_owner_1=Quantum Electronic; legal_owner_2=Devices GmbH; legal_owner_3=CERN-OHL-W-2.0; part_material=Aluminium; revision_index=2.1.0; scale=1 : 1; sheet_number=2 / 3; title=Laser back panel
  Height = 210
  Orientation = 1
  Template = <path>
  Width = 297
FEATURE [TechDraw::DrawViewImage] ActiveView
  Height = 102.4
  ImageFile = <userpath>/.cache/FreeCAD/Cache/FreeCAD_Doc_1d0811a7-c1da-4470-98a3-9f43750157cd_cd324b_797434/PageActiveViewk71wDK.png
  LockPosition = false
  Rotation = 0
  ScaleType = 2
  Width = 128
  X = 78.2043
  Y = 137.47
FEATURE [TechDraw::DrawProjGroupItem] View001  label="Front001"
  CoarseView = false
  Direction = (0,0,-1)
  Focus = 100
  HardHidden = false
  IsoCount = 0
  IsoHidden = false
  IsoVisible = false
  LockPosition = true
  Perspective = false
  Rotation = 0
  RotationVector = (1,0,0)
  ScaleType = 2
  ScrubCount = 1
  SeamHidden = false
  SeamVisible = false
  SmoothHidden = false
  SmoothVisible = true
  Source = -> [Body]
  Type = 0
  X = 0
  XDirection = (-1,-1e-16,0)
  Y = 0
FEATURE [TechDraw::DrawProjGroupItem] ProjItem001  label="Left001"
  CoarseView = false
  Direction = (1,1e-16,-1e-16)
  Focus = 100
  HardHidden = true
  IsoCount = 0
  IsoHidden = false
  IsoVisible = false
  LockPosition = false
  Perspective = false
  Rotation = 0
  RotationVector = (1,0,0)
  ScaleType = 0
  ScrubCount = 1
  SeamHidden = false
  SeamVisible = false
  SmoothHidden = true
  SmoothVisible = true
  Source = -> [Body]
  Type = 1
  X = 57.5
  XDirection = (-1e-16,0,-1)
  Y = 0
FEATURE [TechDraw::DrawProjGroup] ProjGroup001
  Anchor = -> View001
  AutoDistribute = true
  LockPosition = false
  ProjectionType = 0
  Rotation = 0
  ScaleType = 0
  Source = -> [Body]
  Views = -> [View001,ProjItem001]
  X = 145.728
  Y = 152.272
  spacingX = 15
  spacingY = 15
FEATURE [TechDraw::DrawViewDimension] Dimension026
  AngleOverride = false
  Arbitrary = false
  ArbitraryTolerances = false
  BoxCorners = (2) [(-40,-35,0),(40,35,0)]
  EqualTolerance = true
  ExtensionAngle = 0
  FormatSpec = R%.2f
  FormatSpecOverTolerance = %+.2w
  FormatSpecUnderTolerance = %+.2w
  Inverted = false
  LineAngle = 0
  LockPosition = false
  MeasureType = 1
  OverTolerance = 0
  References2D = -> [View001]
  Rotation = 0
  ScaleType = 0
  TheoreticalExact = false
  Type = 4
  UnderTolerance = 0
  X = -42.354
  Y = 41.9562
FEATURE [TechDraw::DrawViewDimension] Dimension027
  AngleOverride = false
  Arbitrary = false
  ArbitraryTolerances = false
  BoxCorners = (2) [(-40,-35,0),(40,35,0)]
  EqualTolerance = true
  ExtensionAngle = 0
  FormatSpec = R%.2f
  FormatSpecOverTolerance = %+.2f
  FormatSpecUnderTolerance = %+.2f
  Inverted = false
  LineAngle = 0
  LockPosition = false
  MeasureType = 1
  OverTolerance = 0
  References2D = -> [View001]
  Rotation = 0
  ScaleType = 0
  TheoreticalExact = false
  Type = 4
  UnderTolerance = 0
  X = -32.61
  Y = 42.2958
FEATURE [TechDraw::DrawViewDimension] Dimension028
  AngleOverride = false
  Arbitrary = false
  ArbitraryTolerances = false
  BoxCorners = (2) [(-2.5,-35,-1e-07),(2.5,35,1e-07)]
  EqualTolerance = true
  ExtensionAngle = 0
  FormatSpec = %.2f
  FormatSpecOverTolerance = %+.2f
  FormatSpecUnderTolerance = %+.2f
  Inverted = false
  LineAngle = 0
  LockPosition = false
  MeasureType = 1
  OverTolerance = 0
  References2D = -> [ProjItem001]
  Rotation = 0
  ScaleType = 0
  TheoreticalExact = false
  Type = 0
  UnderTolerance = 0
  X = -11.9826
  Y = 46.5802
FEATURE [TechDraw::DrawViewDimension] Dimension029
  AngleOverride = false
  Arbitrary = false
  ArbitraryTolerances = false
  BoxCorners = (2) [(-2.5,-35,-1e-07),(2.5,35,1e-07)]
  EqualTolerance = true
  ExtensionAngle = 0
  FormatSpec = %.2f
  FormatSpecOverTolerance = %+.2f
  FormatSpecUnderTolerance = %+.2f
  Inverted = false
  LineAngle = 0
  LockPosition = false
  MeasureType = 1
  OverTolerance = 0
  References2D = -> [ProjItem001]
  Rotation = 0
  ScaleType = 0
  TheoreticalExact = false
  Type = 0
  UnderTolerance = 0
  X = -8.49376
  Y = 41.461
FEATURE [TechDraw::DrawViewDimension] Dimension031
  AngleOverride = false
  Arbitrary = false
  ArbitraryTolerances = false
  BoxCorners = (2) [(-40,-35,0),(40,35,0)]
  EqualTolerance = true
  ExtensionAngle = 0
  FormatSpec = %.2f
  FormatSpecOverTolerance = %+.2f
  FormatSpecUnderTolerance = %+.2f
  Inverted = false
  LineAngle = 0
  LockPosition = false
  MeasureType = 1
  OverTolerance = 0
  References2D = -> [View001]
  Rotation = 0
  ScaleType = 0
  TheoreticalExact = false
  Type = 0
  UnderTolerance = 0
  X = -55.7897
  Y = 24.925
FEATURE [TechDraw::DrawViewDimension] Dimension032
  AngleOverride = false
  Arbitrary = false
  ArbitraryTolerances = false
  BoxCorners = (2) [(-40,-35,0),(40,35,0)]
  EqualTolerance = true
  ExtensionAngle = 0
  FormatSpec = %.2f
  FormatSpecOverTolerance = %+.2f
  FormatSpecUnderTolerance = %+.2f
  Inverted = false
  LineAngle = 0
  LockPosition = false
  MeasureType = 1
  OverTolerance = 0
  References2D = -> [View001]
  Rotation = 0
  ScaleType = 0
  TheoreticalExact = false
  Type = 0
  UnderTolerance = 0
  X = -62.7897
  Y = 17.2625
FEATURE [TechDraw::DrawViewDimension] Dimension033
  AngleOverride = false
  Arbitrary = false
  ArbitraryTolerances = false
  BoxCorners = (2) [(-40,-35,0),(40,35,0)]
  EqualTolerance = true
  ExtensionAngle = 0
  FormatSpec = %.2f
  FormatSpecOverTolerance = %+.2f
  FormatSpecUnderTolerance = %+.2f
  Inverted = false
  LineAngle = 0
  LockPosition = false
  MeasureType = 1
  OverTolerance = 0
  References2D = -> [View001]
  Rotation = 0
  ScaleType = 0
  TheoreticalExact = false
  Type = 0
  UnderTolerance = 0
  X = -55.7897
  Y = 30.075
FEATURE [TechDraw::DrawViewDimension] Dimension034
  AngleOverride = false
  Arbitrary = false
  ArbitraryTolerances = false
  BoxCorners = (2) [(-40,-35,0),(40,35,0)]
  EqualTolerance = true
  ExtensionAngle = 0
  FormatSpec = %.2f
  FormatSpecOverTolerance = %+.2f
  FormatSpecUnderTolerance = %+.2f
  Inverted = false
  LineAngle = 0
  LockPosition = false
  MeasureType = 1
  OverTolerance = 0
  References2D = -> [View001]
  Rotation = 0
  ScaleType = 0
  TheoreticalExact = false
  Type = 0
  UnderTolerance = 0
  X = -69.7897
  Y = 10.7375
FEATURE [TechDraw::DrawViewDimension] Dimension035
  AngleOverride = false
  Arbitrary = false
  ArbitraryTolerances = false
  BoxCorners = (2) [(-40,-35,0),(40,35,0)]
  EqualTolerance = true
  ExtensionAngle = 0
  FormatSpec = %.2f
  FormatSpecOverTolerance = %+.2f
  FormatSpecUnderTolerance = %+.2f
  Inverted = false
  LineAngle = 0
  LockPosition = false
  MeasureType = 1
  OverTolerance = 0
  References2D = -> [View001]
  Rotation = 0
  ScaleType = 0
  TheoreticalExact = false
  Type = 0
  UnderTolerance = 0
  X = -76.7897
  Y = 5.1125
FEATURE [TechDraw::DrawViewDimension] Dimension036
  AngleOverride = false
  Arbitrary = false
  ArbitraryTolerances = false
  BoxCorners = (2) [(-40,-35,0),(40,35,0)]
  EqualTolerance = true
  ExtensionAngle = 0
  FormatSpec = %.2f
  FormatSpecOverTolerance = %+.2f
  FormatSpecUnderTolerance = %+.2f
  Inverted = false
  LineAngle = 0
  LockPosition = false
  MeasureType = 1
  OverTolerance = 0
  References2D = -> [View001]
  Rotation = 0
  ScaleType = 0
  TheoreticalExact = false
  Type = 2
  UnderTolerance = 0
  X = -92.1746
  Y = 0
FEATURE [TechDraw::DrawViewDimension] Dimension037
  AngleOverride = false
  Arbitrary = false
  ArbitraryTolerances = false
  BoxCorners = (2) [(-40,-35,0),(40,35,0)]
  EqualTolerance = true
  ExtensionAngle = 0
  FormatSpec = %.2f
  FormatSpecOverTolerance = %+.2f
  FormatSpecUnderTolerance = %+.2f
  Inverted = false
  LineAngle = 0
  LockPosition = false
  MeasureType = 1
  OverTolerance = 0
  References2D = -> [View001]
  Rotation = 0
  ScaleType = 0
  TheoreticalExact = false
  Type = 0
  UnderTolerance = 0
  X = -47.2173
  Y = -38.8317
FEATURE [TechDraw::DrawViewDimension] Dimension038
  AngleOverride = false
  Arbitrary = false
  ArbitraryTolerances = false
  BoxCorners = (2) [(-40,-35,0),(40,35,0)]
  EqualTolerance = true
  ExtensionAngle = 0
  FormatSpec = %.2f
  FormatSpecOverTolerance = %+.2f
  FormatSpecUnderTolerance = %+.2f
  Inverted = false
  LineAngle = 0
  LockPosition = false
  MeasureType = 1
  OverTolerance = 0
  References2D = -> [View001]
  Rotation = 0
  ScaleType = 0
  TheoreticalExact = false
  Type = 0
  UnderTolerance = 0
  X = -33.375
  Y = -48.0853
FEATURE [TechDraw::DrawViewDimension] Dimension039
  AngleOverride = false
  Arbitrary = false
  ArbitraryTolerances = false
  BoxCorners = (2) [(-40,-35,0),(40,35,0)]
  EqualTolerance = true
  ExtensionAngle = 0
  FormatSpec = %.2f
  FormatSpecOverTolerance = %+.2f
  FormatSpecUnderTolerance = %+.2f
  Inverted = false
  LineAngle = 0
  LockPosition = false
  MeasureType = 1
  OverTolerance = 0
  References2D = -> [View001]
  Rotation = 0
  ScaleType = 0
  TheoreticalExact = false
  Type = 0
  UnderTolerance = 0
  X = -29.5
  Y = -55.0853
FEATURE [TechDraw::DrawViewDimension] Dimension040
  AngleOverride = false
  Arbitrary = false
  ArbitraryTolerances = false
  BoxCorners = (2) [(-40,-35,0),(40,35,0)]
  EqualTolerance = true
  ExtensionAngle = 0
  FormatSpec = %.2f
  FormatSpecOverTolerance = %+.2f
  FormatSpecUnderTolerance = %+.2f
  Inverted = false
  LineAngle = 0
  LockPosition = false
  MeasureType = 1
  OverTolerance = 0
  References2D = -> [View001]
  Rotation = 0
  ScaleType = 0
  TheoreticalExact = false
  Type = 0
  UnderTolerance = 0
  X = -10.5
  Y = -62.0853
FEATURE [TechDraw::DrawViewDimension] Dimension041
  AngleOverride = false
  Arbitrary = false
  ArbitraryTolerances = false
  BoxCorners = (2) [(-40,-35,0),(40,35,0)]
  EqualTolerance = true
  ExtensionAngle = 0
  FormatSpec = %.2f
  FormatSpecOverTolerance = %+.2f
  FormatSpecUnderTolerance = %+.2f
  Inverted = false
  LineAngle = 0
  LockPosition = false
  MeasureType = 1
  OverTolerance = 0
  References2D = -> [View001]
  Rotation = 0
  ScaleType = 0
  TheoreticalExact = false
  Type = 0
  UnderTolerance = 0
  X = -6.625
  Y = -69.0853
FEATURE [TechDraw::DrawViewDimension] Dimension042
  AngleOverride = false
  Arbitrary = false
  ArbitraryTolerances = false
  BoxCorners = (2) [(-40,-35,0),(40,35,0)]
  EqualTolerance = true
  ExtensionAngle = 0
  FormatSpec = %.2f
  FormatSpecOverTolerance = %+.2f
  FormatSpecUnderTolerance = %+.2f
  Inverted = false
  LineAngle = 0
  LockPosition = false
  MeasureType = 1
  OverTolerance = 0
  References2D = -> [View001]
  Rotation = 0
  ScaleType = 0
  TheoreticalExact = false
  Type = 0
  UnderTolerance = 0
  X = -2.5
  Y = -76.0853
FEATURE [TechDraw::DrawViewDimension] Dimension043
  AngleOverride = false
  Arbitrary = false
  ArbitraryTolerances = false
  BoxCorners = (2) [(-40,-35,0),(40,35,0)]
  EqualTolerance = true
  ExtensionAngle = 0
  FormatSpec = %.2f
  FormatSpecOverTolerance = %+.2f
  FormatSpecUnderTolerance = %+.2f
  Inverted = false
  LineAngle = 0
  LockPosition = false
  MeasureType = 1
  OverTolerance = 0
  References2D = -> [View001]
  Rotation = 0
  ScaleType = 0
  TheoreticalExact = false
  Type = 1
  UnderTolerance = 0
  X = 0
  Y = -83.0853
FEATURE [TechDraw::DrawPage] Page001
  KeepUpdated = true
  NextBalloonIndex = 1
  ProjectionType = 0
  Template = -> Template001
  Views = -> [ProjGroup001,Dimension026,Dimension027,Dimension028,Dimension029,Dimension031,Dimension032,Dimension033,Dimension034,Dimension035,Dimension036,Dimension037,Dimension038,Dimension039,Dimension040,Dimension041,Dimension042,Dimension043]
FEATURE [TechDraw::DrawSVGTemplate] Template002
  EditableTexts = approval_person=Patrick Baus; creator=Patrick Baus; date_of_issue=31.08.25; document_type=Component Drawing; general_tolerances=ISO 2768-m; identification_number=DN; language_code=EN; legal_owner_1=Quantum Electronic; legal_owner_2=Devices GmbH; legal_owner_3=CERN-OHL-W-2.0; part_material=Aluminium; revision_index=2.1.0; scale=1 : 1; sheet_number=3 / 3; title=Laser back panel
  Height = 210
  Orientation = 1
  Template = <path>
  Width = 297
FEATURE [TechDraw::DrawProjGroupItem] View002
  CoarseView = false
  Direction = (-7e-16,0,1)
  Focus = 100
  HardHidden = true
  IsoCount = 0
  IsoHidden = false
  IsoVisible = false
  LockPosition = false
  Perspective = false
  Rotation = 0
  RotationVector = (1,0,0)
  ScaleType = 0
  ScrubCount = 1
  SeamHidden = false
  SeamVisible = false
  SmoothHidden = false
  SmoothVisible = true
  Source = -> [Body]
  Type = 0
  X = 133.686
  XDirection = (1,1e-16,7e-16)
  Y = 129.866
FEATURE [TechDraw::DrawViewDimension] Dimension044
  AngleOverride = false
  Arbitrary = false
  ArbitraryTolerances = false
  BoxCorners = (2) [(-40,-35,0),(40,35,0)]
  EqualTolerance = true
  ExtensionAngle = 0
  FormatSpec = ⌀%.2f THRU - DIN 974 - 3,50 x 2,50
  FormatSpecOverTolerance = %+.2f
  FormatSpecUnderTolerance = %+.2f
  Inverted = false
  LineAngle = 0
  LockPosition = false
  MeasureType = 1
  OverTolerance = 0
  References2D = -> [View002]
  Rotation = 0
  ScaleType = 0
  TheoreticalExact = false
  Type = 5
  UnderTolerance = 0
  X = 34.411
  Y = 42.602
FEATURE [TechDraw::DrawViewDimension] Dimension045
  AngleOverride = false
  Arbitrary = false
  ArbitraryTolerances = false
  BoxCorners = (2) [(-40,-35,0),(40,35,0)]
  EqualTolerance = true
  ExtensionAngle = 0
  FormatSpec = %.2f
  FormatSpecOverTolerance = %+.2f
  FormatSpecUnderTolerance = %+.2f
  Inverted = false
  LineAngle = 0
  LockPosition = false
  MeasureType = 1
  OverTolerance = 0
  References2D = -> [View002]
  Rotation = 0
  ScaleType = 0
  TheoreticalExact = false
  Type = 1
  UnderTolerance = 0
  X = 0
  Y = 54.2348
FEATURE [TechDraw::DrawViewAnnotation] Annotation
  Font = osifont
  LineSpace = 100
  LockPosition = false
  MaxWidth = -1
  Rotation = 0
  ScaleType = 0
  Text = Panel cutouts according to: | - DVI: https://www.molex.com/content/dam/molex/molex-dot-com/products/ | automated/en-us/salesdrawingpdf/743/74320/743201004_sd.pdf?inline | -Dsub: https://www.amphenolpcd.com/wp-content/uploads/2023/06/ | Catalog-D-Subs.pdf
  TextSize = 2
  TextStyle = 0
  X = 241.49
  Y = 181.688
FEATURE [TechDraw::DrawViewDimension] Dimension046
  AngleOverride = false
  Arbitrary = false
  ArbitraryTolerances = false
  BoxCorners = (2) [(-40,-35,0),(40,35,0)]
  EqualTolerance = true
  ExtensionAngle = 0
  FormatSpec = %.2f
  FormatSpecOverTolerance = %+.2f
  FormatSpecUnderTolerance = %+.2f
  Inverted = false
  LineAngle = 0
  LockPosition = false
  MeasureType = 1
  OverTolerance = 0
  References2D = -> [View002]
  Rotation = 0
  ScaleType = 0
  TheoreticalExact = false
  Type = 0
  UnderTolerance = 0
  X = 0
  Y = 47.2348
FEATURE [TechDraw::DrawViewDimension] Dimension047
  AngleOverride = false
  Arbitrary = false
  ArbitraryTolerances = false
  BoxCorners = (2) [(-40,-35,0),(40,35,0)]
  EqualTolerance = true
  ExtensionAngle = 0
  FormatSpec = R%.2f
  FormatSpecOverTolerance = %+.2f
  FormatSpecUnderTolerance = %+.2f
  Inverted = false
  LineAngle = 0
  LockPosition = false
  MeasureType = 1
  OverTolerance = 0
  References2D = -> [View002]
  Rotation = 0
  ScaleType = 0
  TheoreticalExact = false
  Type = 4
  UnderTolerance = 0
  X = -23.3287
  Y = 42.9317
FEATURE [TechDraw::DrawViewDimension] Dimension048
  AngleOverride = false
  Arbitrary = false
  ArbitraryTolerances = false
  BoxCorners = (2) [(-40,-35,0),(40,35,0)]
  EqualTolerance = true
  ExtensionAngle = 0
  FormatSpec = R%.2f
  FormatSpecOverTolerance = %+.2f
  FormatSpecUnderTolerance = %+.2f
  Inverted = false
  LineAngle = 0
  LockPosition = false
  MeasureType = 1
  OverTolerance = 0
  References2D = -> [View002]
  Rotation = 0
  ScaleType = 0
  TheoreticalExact = false
  Type = 4
  UnderTolerance = 0
  X = -51.432
  Y = 8.54966
FEATURE [TechDraw::DrawViewDimension] Dimension050
  AngleOverride = false
  Arbitrary = false
  ArbitraryTolerances = false
  BoxCorners = (2) [(-40,-35,0),(40,35,0)]
  EqualTolerance = true
  ExtensionAngle = 0
  FormatSpec = %.2f
  FormatSpecOverTolerance = %+.2f
  FormatSpecUnderTolerance = %+.2f
  Inverted = false
  LineAngle = 0
  LockPosition = false
  MeasureType = 1
  OverTolerance = 0
  References2D = -> [View002]
  Rotation = 0
  ScaleType = 0
  TheoreticalExact = false
  Type = 0
  UnderTolerance = 0
  X = -62.6448
  Y = 27.5
FEATURE [TechDraw::DrawViewDimension] Dimension051
  AngleOverride = false
  Arbitrary = false
  ArbitraryTolerances = false
  BoxCorners = (2) [(-40,-35,0),(40,35,0)]
  EqualTolerance = true
  ExtensionAngle = 0
  FormatSpec = %.2f
  FormatSpecOverTolerance = %+.2f
  FormatSpecUnderTolerance = %+.2f
  Inverted = false
  LineAngle = 0
  LockPosition = false
  MeasureType = 1
  OverTolerance = 0
  References2D = -> [View002]
  Rotation = 0
  ScaleType = 0
  TheoreticalExact = false
  Type = 0
  UnderTolerance = 0
  X = 49.1649
  Y = 20
FEATURE [TechDraw::DrawViewDimension] Dimension052
  AngleOverride = false
  Arbitrary = false
  ArbitraryTolerances = false
  BoxCorners = (2) [(-40,-35,0),(40,35,0)]
  EqualTolerance = true
  ExtensionAngle = 0
  FormatSpec = %.2f
  FormatSpecOverTolerance = %+.2f
  FormatSpecUnderTolerance = %+.2f
  Inverted = false
  LineAngle = 0
  LockPosition = false
  MeasureType = 1
  OverTolerance = 0
  References2D = -> [View002]
  Rotation = 0
  ScaleType = 0
  TheoreticalExact = false
  Type = 0
  UnderTolerance = 0
  X = 49.1649
  Y = -7
FEATURE [TechDraw::DrawViewDimension] Dimension053
  AngleOverride = false
  Arbitrary = false
  ArbitraryTolerances = false
  BoxCorners = (2) [(-40,-35,0),(40,35,0)]
  EqualTolerance = true
  ExtensionAngle = 0
  FormatSpec = R%.2f
  FormatSpecOverTolerance = %+.2f
  FormatSpecUnderTolerance = %+.2f
  Inverted = false
  LineAngle = 0
  LockPosition = false
  MeasureType = 1
  OverTolerance = 0
  References2D = -> [View002]
  Rotation = 0
  ScaleType = 0
  TheoreticalExact = false
  Type = 4
  UnderTolerance = 0
  X = -45.203
  Y = 2.85387
FEATURE [TechDraw::DrawViewDimension] Dimension054
  AngleOverride = false
  Arbitrary = false
  ArbitraryTolerances = false
  BoxCorners = (2) [(-40,-35,0),(40,35,0)]
  EqualTolerance = true
  ExtensionAngle = 0
  FormatSpec = %.2f
  FormatSpecOverTolerance = %+.2f
  FormatSpecUnderTolerance = %+.2f
  Inverted = false
  LineAngle = 0
  LockPosition = false
  MeasureType = 1
  OverTolerance = 0
  References2D = -> [View002]
  Rotation = 0
  ScaleType = 0
  TheoreticalExact = false
  Type = 1
  UnderTolerance = 0
  X = 0
  Y = -41.3616
FEATURE [TechDraw::DrawViewDimension] Dimension055
  AngleOverride = false
  Arbitrary = false
  ArbitraryTolerances = false
  BoxCorners = (2) [(-40,-35,0),(40,35,0)]
  EqualTolerance = true
  ExtensionAngle = 0
  FormatSpec = %.2f
  FormatSpecOverTolerance = %+.2f
  FormatSpecUnderTolerance = %+.2f
  Inverted = false
  LineAngle = 0
  LockPosition = false
  MeasureType = 1
  OverTolerance = 0
  References2D = -> [View002]
  Rotation = 0
  ScaleType = 0
  TheoreticalExact = false
  Type = 6
  UnderTolerance = 0
  X = -1.47848
  Y = 0.09314
FEATURE [TechDraw::DrawViewDimension] Dimension056
  AngleOverride = false
  Arbitrary = false
  ArbitraryTolerances = false
  BoxCorners = (2) [(-40,-35,0),(40,35,0)]
  EqualTolerance = true
  ExtensionAngle = 0
  FormatSpec = %.2f
  FormatSpecOverTolerance = %+.2f
  FormatSpecUnderTolerance = %+.2f
  Inverted = false
  LineAngle = 0
  LockPosition = false
  MeasureType = 1
  OverTolerance = 0
  References2D = -> [View002]
  Rotation = 0
  ScaleType = 0
  TheoreticalExact = false
  Type = 0
  UnderTolerance = 0
  X = -69.6448
  Y = 14
FEATURE [TechDraw::DrawPage] Page002
  KeepUpdated = true
  NextBalloonIndex = 1
  ProjectionType = 0
  Template = -> Template002
  Views = -> [View002,Dimension044,Dimension045,Annotation,Dimension046,Dimension047,Dimension048,Dimension050,Dimension051,Dimension052,Dimension053,Dimension054,Dimension055,Dimension056]
FEATURE [TechDraw::DrawViewSymbol] Symbol
  LockPosition = false
  Rotation = 0
  Scale = 0.1
  ScaleType = 2
  Symbol = <blob: 7288 chars omitted>
  X = 93.6157
  Y = 30.2942
FEATURE [TechDraw::DrawPage] Page
  KeepUpdated = true
  NextBalloonIndex = 1
  ProjectionType = 0
  Template = -> Template
  Views = -> [Dimension008,Dimension009,Dimension012,Dimension013,Dimension,Dimension014,Dimension015,Dimension016,Dimension017,Dimension018,Dimension019,Dimension020,Dimension021,ProjGroup,Dimension023,Dimension024,Dimension025,ActiveView,Symbol]
note: 3 file-system paths scrubbed to <path> (originals preserved in the JSON sidecar)
